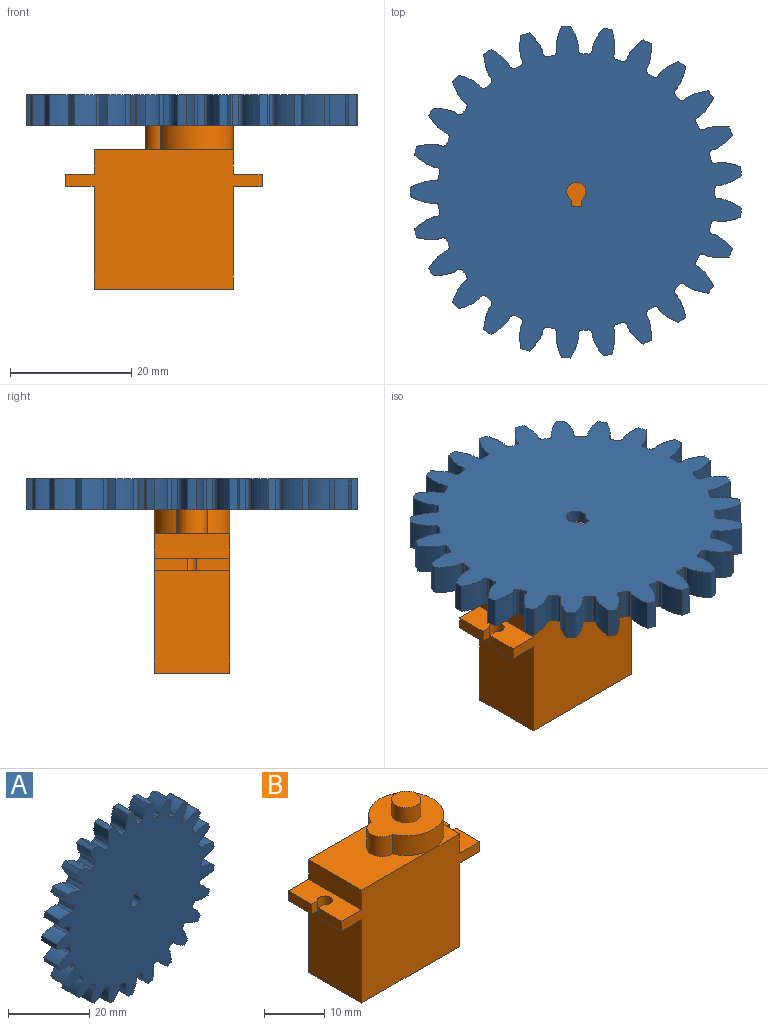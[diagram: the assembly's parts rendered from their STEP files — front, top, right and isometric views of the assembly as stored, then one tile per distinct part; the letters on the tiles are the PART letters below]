
ASSEMBLY  parts=2 mates=1
PART A: 156 faces, bbox 54.7x5.1x54.8 mm
  f0: cylinder r=27.43mm len=5.08mm, axis (0,1,0), area 7.4mm2, adj f24,f30,f141,f153
  f1: cylinder r=27.43mm len=5.08mm, axis (0,1,0), area 7.4mm2, adj f24,f30,f148,f151
  f2: cylinder r=27.43mm len=5.08mm, axis (0,1,0), area 7.4mm2, adj f24,f30,f136,f143
  f3: cylinder r=27.43mm len=5.08mm, axis (0,1,0), area 7.4mm2, adj f24,f30,f131,f138
  f4: cylinder r=27.43mm len=5.08mm, axis (0,1,0), area 7.4mm2, adj f24,f30,f126,f133
  f5: cylinder r=27.43mm len=5.08mm, axis (0,1,0), area 7.4mm2, adj f24,f30,f116,f128
  f6: cylinder r=27.43mm len=5.08mm, axis (0,1,0), area 7.4mm2, adj f24,f30,f111,f123
  f7: cylinder r=27.43mm len=5.08mm, axis (0,1,0), area 7.4mm2, adj f24,f30,f118,f121
  f8: cylinder r=27.43mm len=5.08mm, axis (0,1,0), area 7.4mm2, adj f24,f30,f106,f113
  f9: cylinder r=27.43mm len=5.08mm, axis (0,1,0), area 7.4mm2, adj f24,f30,f101,f108
  f10: cylinder r=27.43mm len=5.08mm, axis (0,1,0), area 7.4mm2, adj f24,f30,f96,f103
  f11: cylinder r=27.43mm len=5.08mm, axis (0,1,0), area 7.4mm2, adj f24,f30,f81,f98
  f12: cylinder r=27.43mm len=5.08mm, axis (0,1,0), area 7.4mm2, adj f24,f30,f31,f93
  f13: cylinder r=27.43mm len=5.08mm, axis (0,1,0), area 7.4mm2, adj f24,f30,f88,f91
  f14: cylinder r=27.43mm len=5.08mm, axis (0,1,0), area 7.4mm2, adj f24,f30,f76,f83
  f15: cylinder r=27.43mm len=5.08mm, axis (0,1,0), area 7.4mm2, adj f24,f30,f78,f86
  f16: cylinder r=27.43mm len=5.08mm, axis (0,1,0), area 7.4mm2, adj f24,f30,f73,f146
  f17: cylinder r=27.43mm len=5.08mm, axis (0,1,0), area 7.4mm2, adj f24,f30,f68,f71
  f18: cylinder r=27.43mm len=5.08mm, axis (0,1,0), area 7.4mm2, adj f24,f30,f63,f66
  f19: cylinder r=27.43mm len=5.08mm, axis (0,1,0), area 7.4mm2, adj f24,f30,f58,f61
  f20: cylinder r=27.43mm len=5.08mm, axis (0,1,0), area 7.4mm2, adj f24,f30,f46,f53
  f21: cylinder r=27.43mm len=5.08mm, axis (0,1,0), area 7.4mm2, adj f24,f30,f36,f48
  f22: cylinder r=27.43mm len=5.08mm, axis (0,1,0), area 7.4mm2, adj f24,f30,f43,f56
  f23: cylinder r=27.43mm len=5.08mm, axis (0,1,0), area 7.4mm2, adj f24,f30,f38,f41
  f24: plane 54.85x54.74mm, normal (0,-1,0), area 1985mm2, adj f0,f1,f2,f3,f4,f5,f6,f7
  f25: plane 5.08x1.01mm, normal (-1,0,0), area 5.1mm2, adj f24,f26,f28,f30
  f26: cylinder r=1.59mm len=5.08mm, axis (0,1,0), area 42.2mm2, adj f24,f25,f27,f30
  f27: plane 5.08x1.01mm, normal (1,0,0), area 5.1mm2, adj f24,f26,f28,f30
  f28: plane 5.08x1.59mm, normal (0,0,-1), area 8.1mm2, adj f24,f25,f27,f30
  f29: cylinder r=27.43mm len=5.08mm, axis (0,1,0), area 7.4mm2, adj f24,f30,f33,f51
  f30: plane 54.85x54.74mm, normal (0,1,0), area 1985mm2, adj f0,f1,f2,f3,f4,f5,f6,f7
  f31: extruded ~5.08x3.89mm, area 21.7mm2, adj f12,f24,f30,f34
  f32: cylinder r=22.86mm len=5.08mm, axis (0,1,0), area 5.4mm2, adj f24,f30,f34,f35
  f33: extruded ~5.08x3.89mm, area 21.7mm2, adj f24,f29,f30,f35
  f34: cylinder r=0.58mm len=5.08mm, axis (0,1,0), area 4.5mm2, adj f24,f30,f31,f32
  f35: cylinder r=0.58mm len=5.08mm, axis (0,1,0), area 4.5mm2, adj f24,f30,f32,f33
  f36: extruded ~5.08x3.93mm, area 21.7mm2, adj f21,f24,f30,f39
  f37: cylinder r=22.86mm len=5.08mm, axis (0,1,0), area 5.4mm2, adj f24,f30,f39,f40
  f38: extruded ~5.08x3.83mm, area 21.7mm2, adj f23,f24,f30,f40
  f39: cylinder r=0.58mm len=5.08mm, axis (0,1,0), area 4.5mm2, adj f24,f30,f36,f37
  f40: cylinder r=0.58mm len=5.08mm, axis (0,1,0), area 4.5mm2, adj f24,f30,f37,f38
  f41: extruded ~5.08x3.43mm, area 21.7mm2, adj f23,f24,f30,f44
  f42: cylinder r=22.86mm len=5.08mm, axis (0,1,0), area 5.4mm2, adj f24,f30,f44,f45
  f43: extruded ~5.08x4.14mm, area 21.7mm2, adj f22,f24,f30,f45
  f44: cylinder r=0.58mm len=5.08mm, axis (0,1,0), area 4.5mm2, adj f24,f30,f41,f42
  f45: cylinder r=0.58mm len=5.08mm, axis (0,1,0), area 4.5mm2, adj f24,f30,f42,f43
  f46: extruded ~5.08x4.18mm, area 21.7mm2, adj f20,f24,f30,f49
  f47: cylinder r=22.86mm len=5.08mm, axis (0,1,0), area 5.4mm2, adj f24,f30,f49,f50
  f48: extruded ~5.08x3.27mm, area 21.7mm2, adj f21,f24,f30,f50
  f49: cylinder r=0.58mm len=5.08mm, axis (0,1,0), area 4.5mm2, adj f24,f30,f46,f47
  f50: cylinder r=0.58mm len=5.08mm, axis (0,1,0), area 4.5mm2, adj f24,f30,f47,f48
  f51: extruded ~5.08x4.17mm, area 21.7mm2, adj f24,f29,f30,f54
  f52: cylinder r=22.86mm len=5.08mm, axis (0,1,0), area 5.4mm2, adj f24,f30,f54,f55
  f53: extruded ~5.08x3.38mm, area 21.7mm2, adj f20,f24,f30,f55
  f54: cylinder r=0.58mm len=5.08mm, axis (0,1,0), area 4.5mm2, adj f24,f30,f51,f52
  f55: cylinder r=0.58mm len=5.08mm, axis (0,1,0), area 4.5mm2, adj f24,f30,f52,f53
  f56: extruded ~5.08x3.21mm, area 21.7mm2, adj f22,f24,f30,f59
  f57: cylinder r=22.86mm len=5.08mm, axis (0,1,0), area 5.4mm2, adj f24,f30,f59,f60
  f58: extruded ~5.08x4.2mm, area 21.7mm2, adj f19,f24,f30,f60
  f59: cylinder r=0.58mm len=5.08mm, axis (0,1,0), area 4.5mm2, adj f24,f30,f56,f57
  f60: cylinder r=0.58mm len=5.08mm, axis (0,1,0), area 4.5mm2, adj f24,f30,f57,f58
  f61: extruded ~5.08x3.79mm, area 21.7mm2, adj f19,f24,f30,f64
  f62: cylinder r=22.86mm len=5.08mm, axis (0,1,0), area 5.4mm2, adj f24,f30,f64,f65
  f63: extruded ~5.08x3.99mm, area 21.7mm2, adj f18,f24,f30,f65
  f64: cylinder r=0.58mm len=5.08mm, axis (0,1,0), area 4.5mm2, adj f24,f30,f61,f62
  f65: cylinder r=0.58mm len=5.08mm, axis (0,1,0), area 4.5mm2, adj f24,f30,f62,f63
  f66: extruded ~5.08x4.12mm, area 21.7mm2, adj f18,f24,f30,f69
  f67: cylinder r=22.86mm len=5.08mm, axis (0,1,0), area 5.4mm2, adj f24,f30,f69,f70
  f68: extruded ~5.08x3.53mm, area 21.7mm2, adj f17,f24,f30,f70
  f69: cylinder r=0.58mm len=5.08mm, axis (0,1,0), area 4.5mm2, adj f24,f30,f66,f67
  f70: cylinder r=0.58mm len=5.08mm, axis (0,1,0), area 4.5mm2, adj f24,f30,f67,f68
  f71: extruded ~5.08x4.2mm, area 21.7mm2, adj f17,f24,f30,f74
  f72: cylinder r=22.86mm len=5.08mm, axis (0,1,0), area 5.4mm2, adj f24,f30,f74,f75
  f73: extruded ~5.08x3.1mm, area 21.7mm2, adj f16,f24,f30,f75
  f74: cylinder r=0.58mm len=5.08mm, axis (0,1,0), area 4.5mm2, adj f24,f30,f71,f72
  f75: cylinder r=0.58mm len=5.08mm, axis (0,1,0), area 4.5mm2, adj f24,f30,f72,f73
  f76: extruded ~5.08x3.83mm, area 21.7mm2, adj f14,f24,f30,f79
  f77: cylinder r=22.86mm len=5.08mm, axis (0,1,0), area 5.4mm2, adj f24,f30,f79,f80
  f78: extruded ~5.08x3.93mm, area 21.7mm2, adj f15,f24,f30,f80
  f79: cylinder r=0.58mm len=5.08mm, axis (0,1,0), area 4.5mm2, adj f24,f30,f76,f77
  f80: cylinder r=0.58mm len=5.08mm, axis (0,1,0), area 4.5mm2, adj f24,f30,f77,f78
  f81: extruded ~5.08x4.14mm, area 21.7mm2, adj f11,f24,f30,f84
  f82: cylinder r=22.86mm len=5.08mm, axis (0,1,0), area 5.4mm2, adj f24,f30,f84,f85
  f83: extruded ~5.08x3.43mm, area 21.7mm2, adj f14,f24,f30,f85
  f84: cylinder r=0.58mm len=5.08mm, axis (0,1,0), area 4.5mm2, adj f24,f30,f81,f82
  f85: cylinder r=0.58mm len=5.08mm, axis (0,1,0), area 4.5mm2, adj f24,f30,f82,f83
  f86: extruded ~5.08x3.27mm, area 21.7mm2, adj f15,f24,f30,f89
  f87: cylinder r=22.86mm len=5.08mm, axis (0,1,0), area 5.4mm2, adj f24,f30,f89,f90
  f88: extruded ~5.08x4.18mm, area 21.7mm2, adj f13,f24,f30,f90
  f89: cylinder r=0.58mm len=5.08mm, axis (0,1,0), area 4.5mm2, adj f24,f30,f86,f87
  f90: cylinder r=0.58mm len=5.08mm, axis (0,1,0), area 4.5mm2, adj f24,f30,f87,f88
  f91: extruded ~5.08x3.38mm, area 21.7mm2, adj f13,f24,f30,f94
  f92: cylinder r=22.86mm len=5.08mm, axis (0,1,0), area 5.4mm2, adj f24,f30,f94,f95
  f93: extruded ~5.08x4.17mm, area 21.7mm2, adj f12,f24,f30,f95
  f94: cylinder r=0.58mm len=5.08mm, axis (0,1,0), area 4.5mm2, adj f24,f30,f91,f92
  f95: cylinder r=0.58mm len=5.08mm, axis (0,1,0), area 4.5mm2, adj f24,f30,f92,f93
  f96: extruded ~5.08x4.2mm, area 21.7mm2, adj f10,f24,f30,f99
  f97: cylinder r=22.86mm len=5.08mm, axis (0,1,0), area 5.4mm2, adj f24,f30,f99,f100
  f98: extruded ~5.08x3.21mm, area 21.7mm2, adj f11,f24,f30,f100
  f99: cylinder r=0.58mm len=5.08mm, axis (0,1,0), area 4.5mm2, adj f24,f30,f96,f97
  f100: cylinder r=0.58mm len=5.08mm, axis (0,1,0), area 4.5mm2, adj f24,f30,f97,f98
  f101: extruded ~5.08x3.99mm, area 21.7mm2, adj f9,f24,f30,f104
  f102: cylinder r=22.86mm len=5.08mm, axis (0,1,0), area 5.4mm2, adj f24,f30,f104,f105
  f103: extruded ~5.08x3.79mm, area 21.7mm2, adj f10,f24,f30,f105
  f104: cylinder r=0.58mm len=5.08mm, axis (0,1,0), area 4.5mm2, adj f24,f30,f101,f102
  f105: cylinder r=0.58mm len=5.08mm, axis (0,1,0), area 4.5mm2, adj f24,f30,f102,f103
  f106: extruded ~5.08x3.53mm, area 21.7mm2, adj f8,f24,f30,f109
  f107: cylinder r=22.86mm len=5.08mm, axis (0,1,0), area 5.4mm2, adj f24,f30,f109,f110
  f108: extruded ~5.08x4.12mm, area 21.7mm2, adj f9,f24,f30,f110
  f109: cylinder r=0.58mm len=5.08mm, axis (0,1,0), area 4.5mm2, adj f24,f30,f106,f107
  f110: cylinder r=0.58mm len=5.08mm, axis (0,1,0), area 4.5mm2, adj f24,f30,f107,f108
  f111: extruded ~5.08x3.1mm, area 21.7mm2, adj f6,f24,f30,f114
  f112: cylinder r=22.86mm len=5.08mm, axis (0,1,0), area 5.4mm2, adj f24,f30,f114,f115
  f113: extruded ~5.08x4.2mm, area 21.7mm2, adj f8,f24,f30,f115
  f114: cylinder r=0.58mm len=5.08mm, axis (0,1,0), area 4.5mm2, adj f24,f30,f111,f112
  f115: cylinder r=0.58mm len=5.08mm, axis (0,1,0), area 4.5mm2, adj f24,f30,f112,f113
  f116: extruded ~5.08x4.09mm, area 21.7mm2, adj f5,f24,f30,f119
  f117: cylinder r=22.86mm len=5.08mm, axis (0,1,0), area 5.4mm2, adj f24,f30,f119,f120
  f118: extruded ~5.08x3.58mm, area 21.7mm2, adj f7,f24,f30,f120
  f119: cylinder r=0.58mm len=5.08mm, axis (0,1,0), area 4.5mm2, adj f24,f30,f116,f117
  f120: cylinder r=0.58mm len=5.08mm, axis (0,1,0), area 4.5mm2, adj f24,f30,f117,f118
  f121: extruded ~5.08x3.71mm, area 21.7mm2, adj f7,f24,f30,f124
  f122: cylinder r=22.86mm len=5.08mm, axis (0,1,0), area 5.4mm2, adj f24,f30,f124,f125
  f123: extruded ~5.08x4.02mm, area 21.7mm2, adj f6,f24,f30,f125
  f124: cylinder r=0.58mm len=5.08mm, axis (0,1,0), area 4.5mm2, adj f24,f30,f121,f122
  f125: cylinder r=0.58mm len=5.08mm, axis (0,1,0), area 4.5mm2, adj f24,f30,f122,f123
  f126: extruded ~5.08x4.21mm, area 21.7mm2, adj f4,f24,f30,f129
  f127: cylinder r=22.86mm len=5.08mm, axis (0,1,0), area 5.4mm2, adj f24,f30,f129,f130
  f128: extruded ~5.08x3.03mm, area 21.7mm2, adj f5,f24,f30,f130
  f129: cylinder r=0.58mm len=5.08mm, axis (0,1,0), area 4.5mm2, adj f24,f30,f126,f127
  f130: cylinder r=0.58mm len=5.08mm, axis (0,1,0), area 4.5mm2, adj f24,f30,f127,f128
  f131: extruded ~5.08x4.06mm, area 21.7mm2, adj f3,f24,f30,f134
  f132: cylinder r=22.86mm len=5.08mm, axis (0,1,0), area 5.4mm2, adj f24,f30,f134,f135
  f133: extruded ~5.08x3.66mm, area 21.7mm2, adj f4,f24,f30,f135
  f134: cylinder r=0.58mm len=5.08mm, axis (0,1,0), area 4.5mm2, adj f24,f30,f131,f132
  f135: cylinder r=0.58mm len=5.08mm, axis (0,1,0), area 4.5mm2, adj f24,f30,f132,f133
  f136: extruded ~5.08x3.66mm, area 21.7mm2, adj f2,f24,f30,f139
  f137: cylinder r=22.86mm len=5.08mm, axis (0,1,0), area 5.4mm2, adj f24,f30,f139,f140
  f138: extruded ~5.08x4.06mm, area 21.7mm2, adj f3,f24,f30,f140
  f139: cylinder r=0.58mm len=5.08mm, axis (0,1,0), area 4.5mm2, adj f24,f30,f136,f137
  f140: cylinder r=0.58mm len=5.08mm, axis (0,1,0), area 4.5mm2, adj f24,f30,f137,f138
  f141: extruded ~5.08x3.03mm, area 21.7mm2, adj f0,f24,f30,f144
  f142: cylinder r=22.86mm len=5.08mm, axis (0,1,0), area 5.4mm2, adj f24,f30,f144,f145
  f143: extruded ~5.08x4.21mm, area 21.7mm2, adj f2,f24,f30,f145
  f144: cylinder r=0.58mm len=5.08mm, axis (0,1,0), area 4.5mm2, adj f24,f30,f141,f142
  f145: cylinder r=0.58mm len=5.08mm, axis (0,1,0), area 4.5mm2, adj f24,f30,f142,f143
  f146: extruded ~5.08x4.02mm, area 21.7mm2, adj f16,f24,f30,f149
  f147: cylinder r=22.86mm len=5.08mm, axis (0,1,0), area 5.4mm2, adj f24,f30,f149,f150
  f148: extruded ~5.08x3.71mm, area 21.7mm2, adj f1,f24,f30,f150
  f149: cylinder r=0.58mm len=5.08mm, axis (0,1,0), area 4.5mm2, adj f24,f30,f146,f147
  f150: cylinder r=0.58mm len=5.08mm, axis (0,1,0), area 4.5mm2, adj f24,f30,f147,f148
  f151: extruded ~5.08x3.58mm, area 21.7mm2, adj f1,f24,f30,f154
  f152: cylinder r=22.86mm len=5.08mm, axis (0,1,0), area 5.4mm2, adj f24,f30,f154,f155
  f153: extruded ~5.08x4.09mm, area 21.7mm2, adj f0,f24,f30,f155
  f154: cylinder r=0.58mm len=5.08mm, axis (0,1,0), area 4.5mm2, adj f24,f30,f151,f152
  f155: cylinder r=0.58mm len=5.08mm, axis (0,1,0), area 4.5mm2, adj f24,f30,f152,f153
PART B: 29 faces, bbox 32.5x12.6x30 mm
  f0: plane 4.99x4.9mm, normal (0,0,1), area 18.9mm2, adj f1
  f1: cylinder r=2.45mm len=4.9mm, axis (0,0,1), area 46.2mm2, adj f0,f2
  f2: plane 14.61x12.65mm, normal (0,0,1), area 112mm2, adj f1,f3,f4
  f3: cylinder r=2.5mm len=5mm, axis (0,0,1), area 31.6mm2, adj f2,f4,f10
  f4: cylinder r=6.25mm len=12.5mm, axis (0,0,1), area 136.5mm2, adj f2,f3,f8,f10,f11
  f5: plane 2x1.38mm, normal (0,-1,0), area 2.7mm2, adj f6,f9,f13,f15
  f6: cylinder r=1.25mm len=2.5mm, axis (0,0,-1), area 12.5mm2, adj f5,f7,f13,f15
  f7: plane 2x1.38mm, normal (0,1,0), area 2.7mm2, adj f6,f13,f14,f15
  f8: plane 6.25x6.25mm, normal (0,0,1), area 8.4mm2, adj f4,f12,f20
  f9: plane 5.5x2mm, normal (1,0,0), area 11mm2, adj f5,f13,f15,f20
  f10: plane 16.75x12.5mm, normal (0,0,1), area 139.8mm2, adj f3,f4,f18,f20,f22
  f11: plane 6.25x6.25mm, normal (0,0,1), area 8.4mm2, adj f4,f12,f22
  f12: plane 12.5x4mm, normal (1,0,0), area 50mm2, adj f8,f11,f13,f20,f22
  f13: plane 12.5x4.75mm, normal (0,0,1), area 52.7mm2, adj f5,f6,f7,f9,f12,f14,f20,f22
  f14: plane 5.5x2mm, normal (1,0,0), area 11mm2, adj f7,f13,f15,f22
  f15: plane 12.5x4.75mm, normal (0,0,-1), area 52.7mm2, adj f5,f6,f7,f9,f14,f16,f20,f22
  f16: plane 17x12.5mm, normal (1,0,0), area 212.5mm2, adj f15,f17,f20,f22
  f17: plane 23x12.5mm, normal (0,0,-1), area 287.5mm2, adj f16,f20,f21,f22
  f18: plane 12.5x4mm, normal (-1,0,0), area 50mm2, adj f10,f20,f22,f25
  f19: plane 5.5x2mm, normal (-1,0,0), area 11mm2, adj f20,f24,f25,f27
  f20: plane 32.5x23mm, normal (0,1,0), area 548mm2, adj f8,f9,f10,f12,f13,f15,f16,f17
  f21: plane 17x12.5mm, normal (-1,0,0), area 212.5mm2, adj f17,f20,f22,f27
  f22: plane 32.5x23mm, normal (0,-1,0), area 548mm2, adj f10,f11,f12,f13,f14,f15,f16,f17
  f23: plane 5.5x2mm, normal (-1,0,0), area 11mm2, adj f22,f25,f26,f27
  f24: plane 2x1.38mm, normal (0,-1,0), area 2.8mm2, adj f19,f25,f27,f28
  f25: plane 12.5x4.75mm, normal (0,0,1), area 52.7mm2, adj f18,f19,f20,f22,f23,f24,f26,f28
  f26: plane 2x1.38mm, normal (0,1,0), area 2.8mm2, adj f23,f25,f27,f28
  f27: plane 12.5x4.75mm, normal (0,0,-1), area 52.7mm2, adj f19,f20,f21,f22,f23,f24,f26,f28
  f28: cylinder r=1.25mm len=2.5mm, axis (0,0,-1), area 12.5mm2, adj f24,f25,f26,f27
PLACE A rot(axis=(1,0,0),90deg) t=(-6.12,5.73,35.08)mm
PLACE B t=(0.64,-0.52,3)mm
MATE fastened A.f0 <-> B.f2  axis (0,0,-1) through (-6.12,5.73,30)mm
